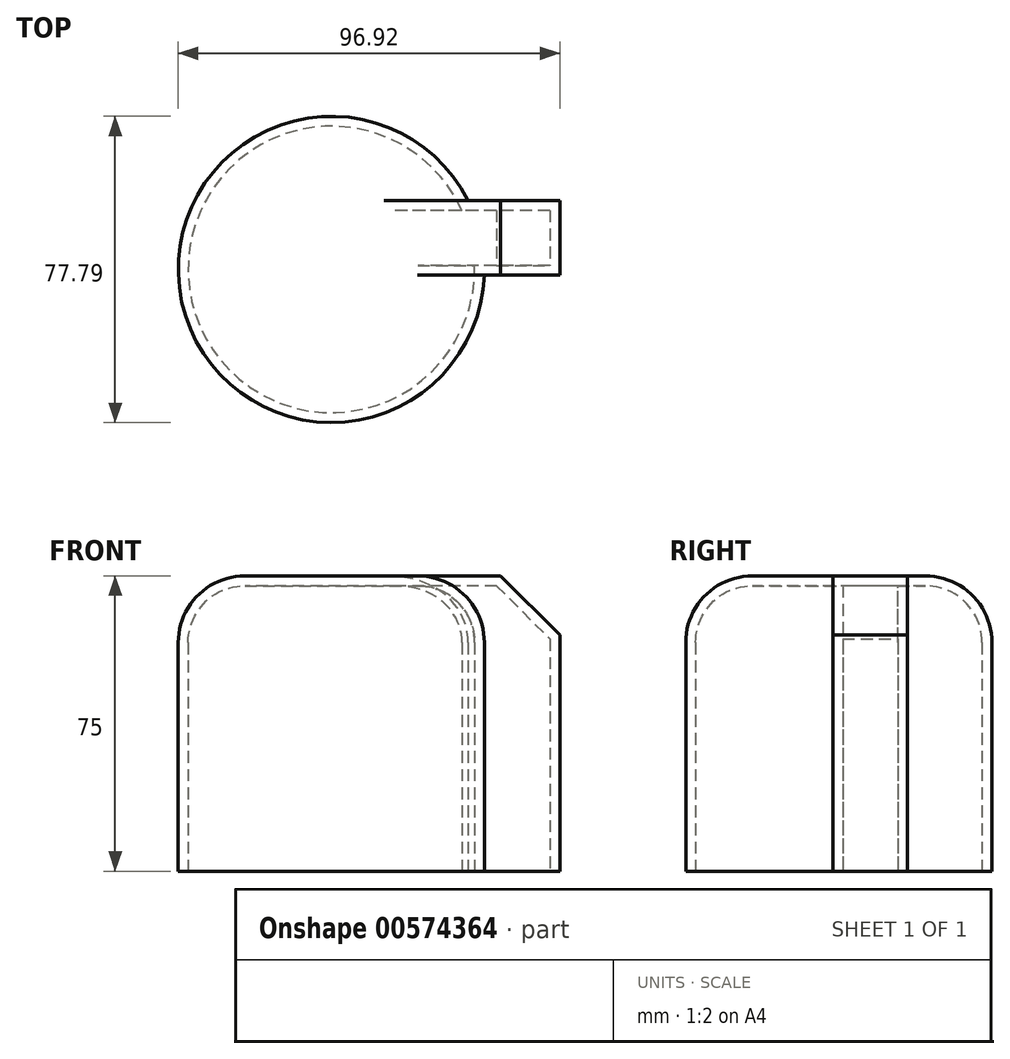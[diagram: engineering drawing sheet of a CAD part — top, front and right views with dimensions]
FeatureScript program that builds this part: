
annotation { "Feature Type Name" : "Feature", "Feature Type Description" : "" }
export const myFeature = defineFeature(function(context is Context, id is Id, definition is map)
    precondition{}
    {
        {
            var Q0;
            Q0=qCreatedBy(makeId("Top.planeOp"),FACE);
            var sketch = newSketch(context, id + "F0", { "sketchPlane" : qUnion([Q0])});
            skCircle(sketch, "E0", {"center": v(-27.53, 19.24) * mm, "radius": 38.9 * mm});
            skLineSegment(sketch, "E1.bottom", {"start": v(30.5, 36.71) * mm, "end": v(-10.66, 36.71) * mm});
            skLineSegment(sketch, "E1.top", {"start": v(30.5, 17.76) * mm, "end": v(-10.66, 17.76) * mm});
            skLineSegment(sketch, "E1.left", {"start": v(30.5, 36.71) * mm, "end": v(30.5, 17.76) * mm});
            skLineSegment(sketch, "E1.right", {"start": v(-10.66, 36.71) * mm, "end": v(-10.66, 17.76) * mm});
            skSolve(sketch);
        }
        {
            var Q0;
            {var subQ5=sQuery(id+"F0.wireOp",EDGE,"E1.right");Q0=makeQuery(id+"F0.imprint","IMPRINT",FACE,{"disambiguationData":[TD([[makeQuery(id+"F0.imprint","IMPRINT",EDGE,{"derivedFrom":subQ5}),1.0]])]});}
            var Q1;
            {var subQ5=sQuery(id+"F0.wireOp",EDGE,"E1.left");Q1=makeQuery(id+"F0.imprint","IMPRINT",FACE,{"disambiguationData":[TD([[makeQuery(id+"F0.imprint","IMPRINT",EDGE,{"derivedFrom":subQ5}),-1.0]])]});}
            var Q2;
            {var subQ5=sQuery(id+"F0.wireOp",EDGE,"E1.right");Q2=makeQuery(id+"F0.imprint","IMPRINT",FACE,{"disambiguationData":[TD([[makeQuery(id+"F0.imprint","IMPRINT",EDGE,{"derivedFrom":subQ5}),-1.0]])]});}
            extrude(context, id + "F1", {"entities" : qUnion([Q0, Q1, Q2]), "depth" : 75 * mm, "offsetDistance" : 25 * mm});
        }
        {
            var Q0;
            Q0=makeQuery(id+"F1.opExtrude","CAP_EDGE",EDGE,{"disambiguationData":[OSD([sQuery(id+"F0.wireOp",EDGE,"E0")])],"isStart":false});
            fillet(context, id + "F2", {"entities" : qUnion([Q0]), "radius" : 16.9 * mm, "tangentPropagation" : true, "allowEdgeOverflow" : false});
        }
        {
            var Q0;
            Q0=makeQuery(id+"F1.opExtrude","CAP_EDGE",EDGE,{"disambiguationData":[OSD([sQuery(id+"F0.wireOp",EDGE,"E1.left")])],"isStart":false});
            chamfer(context, id + "F3", {"entities" : qUnion([Q0]), "width" : 15 * mm, "tangentPropagation" : true});
        }
        {
            var Q0;
            Q0=makeQuery(id+"F1.opExtrude","CAP_FACE",FACE,{"disambiguationData":[OSD([sQuery(id+"F0.wireOp",EDGE,"E0"),sQuery(id+"F0.wireOp",EDGE,"E1.bottom"),sQuery(id+"F0.wireOp",EDGE,"E1.top"),sQuery(id+"F0.wireOp",EDGE,"E1.left")])],"isStart":true});
            shell(context, id + "F4", {"entities" : qUnion([Q0]), "thickness" : 2.5 * mm});
        }
    });
